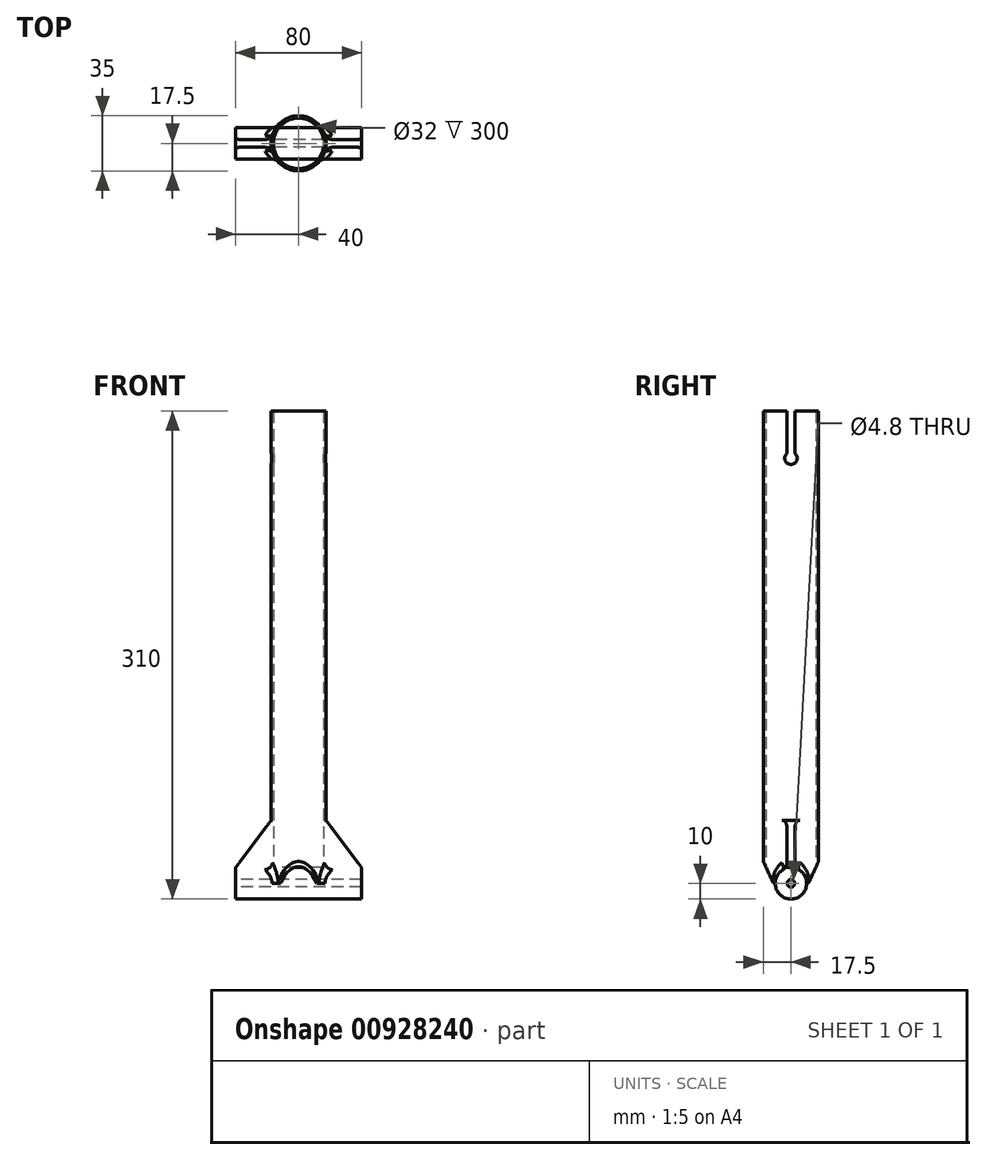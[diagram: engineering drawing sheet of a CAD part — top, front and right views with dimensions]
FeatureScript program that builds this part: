
annotation { "Feature Type Name" : "Feature", "Feature Type Description" : "" }
export const myFeature = defineFeature(function(context is Context, id is Id, definition is map)
    precondition{}
    {
        {
            var Q0;
            Q0=qCreatedBy(makeId("Right.planeOp"),FACE);
            var sketch = newSketch(context, id + "F0", { "sketchPlane" : qUnion([Q0])});
            skCircle(sketch, "E0", {"center": v(0, 0) * mm, "radius": 10 * mm});
            skSolve(sketch);
        }
        {
            var Q0;
            Q0=qCreatedBy(makeId("Top.planeOp"),FACE);
            var sketch = newSketch(context, id + "F1", { "sketchPlane" : qUnion([Q0])});
            skCircle(sketch, "E1", {"center": v(0, 0) * mm, "radius": 17.5 * mm});
            skCircle(sketch, "E2", {"center": v(0, 0) * mm, "radius": 16 * mm});
            skSolve(sketch);
        }
        {
            var Q0;
            Q0=qCreatedBy(makeId("Front.planeOp"),FACE);
            var sketch = newSketch(context, id + "F2", { "sketchPlane" : qUnion([Q0])});
            skLineSegment(sketch, "E3", {"start": v(-40, 9) * mm, "end": v(-16.45, 9) * mm});
            skLineSegment(sketch, "E4", {"start": v(-16.45, 9) * mm, "end": v(-16.45, 40) * mm});
            skLineSegment(sketch, "E5", {"start": v(-16.45, 40) * mm, "end": v(-17.45, 40) * mm});
            skLineSegment(sketch, "E6", {"start": v(-17.45, 40) * mm, "end": v(-40, 10) * mm});
            skLineSegment(sketch, "E7", {"start": v(-40, 10) * mm, "end": v(-40, 9) * mm});
            skLineSegment(sketch, "E8.MirrorCS", {"start": v(17.45, 40) * mm, "end": v(40, 10) * mm});
            skLineSegment(sketch, "E9.MirrorCS", {"start": v(16.45, 40) * mm, "end": v(17.45, 40) * mm});
            skLineSegment(sketch, "E10.MirrorCS", {"start": v(16.45, 9) * mm, "end": v(16.45, 40) * mm});
            skLineSegment(sketch, "E11.MirrorCS", {"start": v(40, 9) * mm, "end": v(16.45, 9) * mm});
            skLineSegment(sketch, "E12.MirrorCS", {"start": v(40, 10) * mm, "end": v(40, 9) * mm});
            skSolve(sketch);
        }
        {
            var Q0;
            Q0=qCreatedBy(makeId("Right.planeOp"),FACE);
            var sketch = newSketch(context, id + "F3", { "sketchPlane" : qUnion([Q0])});
            skArc(sketch, "E13", {"start": v(-9.06, -4.23) * mm, "mid": v(0, -10) * mm, "end": v(9.06, -4.23) * mm});
            skLineSegment(sketch, "E14", {"start": v(9.06, -4.23) * mm, "end": v(21.74, 22.96) * mm});
            skLineSegment(sketch, "E15", {"start": v(-9.06, -4.23) * mm, "end": v(-21.74, 22.96) * mm});
            skLineSegment(sketch, "E16.0", {"start": v(-18.13, -8.45) * mm, "end": v(-30.8, 18.74) * mm});
            skArc(sketch, "E16.1", {"start": v(-18.13, -8.45) * mm, "mid": v(0, -20) * mm, "end": v(18.13, -8.45) * mm});
            skLineSegment(sketch, "E16.2", {"start": v(18.13, -8.45) * mm, "end": v(30.8, 18.74) * mm});
            skLineSegment(sketch, "E17", {"start": v(-30.8, 18.74) * mm, "end": v(-21.74, 22.96) * mm});
            skLineSegment(sketch, "E18", {"start": v(21.74, 22.96) * mm, "end": v(30.8, 18.74) * mm});
            skSolve(sketch);
        }
        {
            var Q0;
            Q0=qCreatedBy(makeId("Right.planeOp"),FACE);
            var sketch = newSketch(context, id + "F4", { "sketchPlane" : qUnion([Q0])});
            skCircle(sketch, "E19", {"center": v(0, 0) * mm, "radius": 2.4 * mm});
            skSolve(sketch);
        }
        {
            var Q0;
            Q0=qCreatedBy(makeId("Right.planeOp"),FACE);
            var sketch = newSketch(context, id + "F5", { "sketchPlane" : qUnion([Q0])});
            skArc(sketch, "E20", {"start": v(-2.5, 273.12) * mm, "mid": v(0, 266) * mm, "end": v(2.5, 273.12) * mm});
            skArc(sketch, "E21.0.endCap", {"start": v(-2.5, 310) * mm, "mid": v(0, 312.5) * mm, "end": v(2.5, 310) * mm});
            skLineSegment(sketch, "E21.0.left", {"start": v(-2.5, 273.12) * mm, "end": v(-2.5, 310) * mm});
            skLineSegment(sketch, "E21.0.right", {"start": v(2.5, 273.12) * mm, "end": v(2.5, 310) * mm});
            skSolve(sketch);
        }
        {
            var Q0;
            Q0=qSketchRegion(id+"F0",true);
            extrude(context, id + "F6", {"entities" : qUnion([Q0]), "endBound" : BoundingType.SYMMETRIC, "depth" : 80 * mm, "offsetDistance" : 25 * mm});
        }
        {
            var Q0;
            Q0=qSketchRegion(id+"F1",true);
            extrude(context, id + "F7", {"entities" : qUnion([Q0]), "operationType" : NewBodyOperationType.ADD, "depth" : 300 * mm, "offsetDistance" : 25 * mm});
        }
        {
            var Q0;
            Q0=qSketchRegion(id+"F2",true);
            extrude(context, id + "F8", {"entities" : qUnion([Q0]), "operationType" : NewBodyOperationType.ADD, "endBound" : BoundingType.SYMMETRIC, "depth" : 5 * mm, "offsetDistance" : 25 * mm});
        }
        {
            var Q0;
            Q0=qSketchRegion(id+"F3",true);
            extrude(context, id + "F9", {"entities" : qUnion([Q0]), "operationType" : NewBodyOperationType.REMOVE, "endBound" : BoundingType.SYMMETRIC, "depth" : 80 * mm, "offsetDistance" : 25 * mm});
        }
        {
            var Q0;
            Q0=qSketchRegion(id+"F4",true);
            extrude(context, id + "F10", {"entities" : qUnion([Q0]), "operationType" : NewBodyOperationType.REMOVE, "endBound" : BoundingType.SYMMETRIC, "depth" : 80 * mm, "offsetDistance" : 25 * mm});
        }
        {
            var Q0;
            Q0=makeQuery(id+"F8.boolean.opBoolean","INTERSECT",EDGE,{"derivedFrom":[makeQuery(id+"F7.opExtrude","SWEPT_FACE",FACE,{"disambiguationData":[OSD([sQuery(id+"F1.wireOp",EDGE,"E1")])]}),makeQuery(id+"F8.opExtrude","CAP_FACE",FACE,{"disambiguationData":[OSD([sQuery(id+"F2.wireOp",EDGE,"E8.MirrorCS"),sQuery(id+"F2.wireOp",EDGE,"E9.MirrorCS"),sQuery(id+"F2.wireOp",EDGE,"E10.MirrorCS"),sQuery(id+"F2.wireOp",EDGE,"E11.MirrorCS"),sQuery(id+"F2.wireOp",EDGE,"E12.MirrorCS")])],"isStart":false})]});
            var Q1;
            Q1=makeQuery(id+"F8.boolean.opBoolean","INTERSECT",EDGE,{"derivedFrom":[makeQuery(id+"F6.opExtrude","SWEPT_FACE",FACE,{"disambiguationData":[OSD([sQuery(id+"F0.wireOp",EDGE,"E0")])]}),makeQuery(id+"F8.opExtrude","CAP_FACE",FACE,{"disambiguationData":[OSD([sQuery(id+"F2.wireOp",EDGE,"E8.MirrorCS"),sQuery(id+"F2.wireOp",EDGE,"E9.MirrorCS"),sQuery(id+"F2.wireOp",EDGE,"E10.MirrorCS"),sQuery(id+"F2.wireOp",EDGE,"E11.MirrorCS"),sQuery(id+"F2.wireOp",EDGE,"E12.MirrorCS")])],"isStart":false})]});
            var Q2;
            Q2=makeQuery(id+"F8.boolean.opBoolean","INTERSECT",EDGE,{"derivedFrom":[makeQuery(id+"F7.opExtrude","SWEPT_FACE",FACE,{"disambiguationData":[OSD([sQuery(id+"F1.wireOp",EDGE,"E1")])]}),makeQuery(id+"F8.opExtrude","CAP_FACE",FACE,{"disambiguationData":[OSD([sQuery(id+"F2.wireOp",EDGE,"E8.MirrorCS"),sQuery(id+"F2.wireOp",EDGE,"E9.MirrorCS"),sQuery(id+"F2.wireOp",EDGE,"E10.MirrorCS"),sQuery(id+"F2.wireOp",EDGE,"E11.MirrorCS"),sQuery(id+"F2.wireOp",EDGE,"E12.MirrorCS")])],"isStart":true})]});
            var Q3;
            Q3=makeQuery(id+"F8.boolean.opBoolean","INTERSECT",EDGE,{"derivedFrom":[makeQuery(id+"F6.opExtrude","SWEPT_FACE",FACE,{"disambiguationData":[OSD([sQuery(id+"F0.wireOp",EDGE,"E0")])]}),makeQuery(id+"F8.opExtrude","CAP_FACE",FACE,{"disambiguationData":[OSD([sQuery(id+"F2.wireOp",EDGE,"E8.MirrorCS"),sQuery(id+"F2.wireOp",EDGE,"E9.MirrorCS"),sQuery(id+"F2.wireOp",EDGE,"E10.MirrorCS"),sQuery(id+"F2.wireOp",EDGE,"E11.MirrorCS"),sQuery(id+"F2.wireOp",EDGE,"E12.MirrorCS")])],"isStart":true})]});
            var Q4;
            Q4=makeQuery(id+"F8.boolean.opBoolean","INTERSECT",EDGE,{"derivedFrom":[makeQuery(id+"F6.opExtrude","SWEPT_FACE",FACE,{"disambiguationData":[OSD([sQuery(id+"F0.wireOp",EDGE,"E0")])]}),makeQuery(id+"F8.opExtrude","CAP_FACE",FACE,{"disambiguationData":[OSD([sQuery(id+"F2.wireOp",EDGE,"E3"),sQuery(id+"F2.wireOp",EDGE,"E4"),sQuery(id+"F2.wireOp",EDGE,"E5"),sQuery(id+"F2.wireOp",EDGE,"E6"),sQuery(id+"F2.wireOp",EDGE,"E7")])],"isStart":true})]});
            var Q5;
            Q5=makeQuery(id+"F8.boolean.opBoolean","INTERSECT",EDGE,{"derivedFrom":[makeQuery(id+"F7.opExtrude","SWEPT_FACE",FACE,{"disambiguationData":[OSD([sQuery(id+"F1.wireOp",EDGE,"E1")])]}),makeQuery(id+"F8.opExtrude","CAP_FACE",FACE,{"disambiguationData":[OSD([sQuery(id+"F2.wireOp",EDGE,"E3"),sQuery(id+"F2.wireOp",EDGE,"E4"),sQuery(id+"F2.wireOp",EDGE,"E5"),sQuery(id+"F2.wireOp",EDGE,"E6"),sQuery(id+"F2.wireOp",EDGE,"E7")])],"isStart":true})]});
            var Q6;
            Q6=makeQuery(id+"F8.boolean.opBoolean","INTERSECT",EDGE,{"derivedFrom":[makeQuery(id+"F7.opExtrude","SWEPT_FACE",FACE,{"disambiguationData":[OSD([sQuery(id+"F1.wireOp",EDGE,"E1")])]}),makeQuery(id+"F8.opExtrude","CAP_FACE",FACE,{"disambiguationData":[OSD([sQuery(id+"F2.wireOp",EDGE,"E3"),sQuery(id+"F2.wireOp",EDGE,"E4"),sQuery(id+"F2.wireOp",EDGE,"E5"),sQuery(id+"F2.wireOp",EDGE,"E6"),sQuery(id+"F2.wireOp",EDGE,"E7")])],"isStart":false})]});
            var Q7;
            Q7=makeQuery(id+"F8.boolean.opBoolean","INTERSECT",EDGE,{"derivedFrom":[makeQuery(id+"F6.opExtrude","SWEPT_FACE",FACE,{"disambiguationData":[OSD([sQuery(id+"F0.wireOp",EDGE,"E0")])]}),makeQuery(id+"F8.opExtrude","CAP_FACE",FACE,{"disambiguationData":[OSD([sQuery(id+"F2.wireOp",EDGE,"E3"),sQuery(id+"F2.wireOp",EDGE,"E4"),sQuery(id+"F2.wireOp",EDGE,"E5"),sQuery(id+"F2.wireOp",EDGE,"E6"),sQuery(id+"F2.wireOp",EDGE,"E7")])],"isStart":false})]});
            var Q8;
            {var subQ0=makeQuery(id+"F6.opExtrude","SWEPT_FACE",FACE,{"disambiguationData":[OSD([sQuery(id+"F0.wireOp",EDGE,"E0")])]});var subQ1=sQuery(id+"F1.wireOp",EDGE,"E1");var subQ2=makeQuery(id+"F7.opExtrude","SWEPT_FACE",FACE,{"disambiguationData":[OSD([subQ1])]});Q8=makeQuery(id+"F8.boolean.opBoolean","SPLIT",EDGE,{"disambiguationData":[TD([makeQuery(id+"F8.opExtrude","CAP_FACE",FACE,{"disambiguationData":[OSD([sQuery(id+"F2.wireOp",EDGE,"E3"),sQuery(id+"F2.wireOp",EDGE,"E4"),sQuery(id+"F2.wireOp",EDGE,"E5"),sQuery(id+"F2.wireOp",EDGE,"E6"),sQuery(id+"F2.wireOp",EDGE,"E7")])],"isStart":true})])],"derivedFrom":makeQuery(id+"F7.boolean.opBoolean","INTERSECT",EDGE,{"disambiguationData":[OD(0.0)],"derivedFrom":[subQ0,subQ2]})});}
            var Q9;
            {var subQ0=makeQuery(id+"F6.opExtrude","SWEPT_FACE",FACE,{"disambiguationData":[OSD([sQuery(id+"F0.wireOp",EDGE,"E0")])]});var subQ1=sQuery(id+"F1.wireOp",EDGE,"E1");var subQ2=makeQuery(id+"F7.opExtrude","SWEPT_FACE",FACE,{"disambiguationData":[OSD([subQ1])]});Q9=makeQuery(id+"F8.boolean.opBoolean","SPLIT",EDGE,{"disambiguationData":[TD([makeQuery(id+"F8.opExtrude","CAP_FACE",FACE,{"disambiguationData":[OSD([sQuery(id+"F2.wireOp",EDGE,"E8.MirrorCS"),sQuery(id+"F2.wireOp",EDGE,"E9.MirrorCS"),sQuery(id+"F2.wireOp",EDGE,"E10.MirrorCS"),sQuery(id+"F2.wireOp",EDGE,"E11.MirrorCS"),sQuery(id+"F2.wireOp",EDGE,"E12.MirrorCS")])],"isStart":true})])],"derivedFrom":makeQuery(id+"F7.boolean.opBoolean","INTERSECT",EDGE,{"disambiguationData":[OD(1.0)],"derivedFrom":[subQ0,subQ2]})});}
            var Q10;
            {var subQ0=makeQuery(id+"F6.opExtrude","SWEPT_FACE",FACE,{"disambiguationData":[OSD([sQuery(id+"F0.wireOp",EDGE,"E0")])]});var subQ1=sQuery(id+"F1.wireOp",EDGE,"E1");var subQ2=makeQuery(id+"F7.opExtrude","SWEPT_FACE",FACE,{"disambiguationData":[OSD([subQ1])]});Q10=makeQuery(id+"F8.boolean.opBoolean","SPLIT",EDGE,{"disambiguationData":[TD([makeQuery(id+"F8.opExtrude","CAP_FACE",FACE,{"disambiguationData":[OSD([sQuery(id+"F2.wireOp",EDGE,"E8.MirrorCS"),sQuery(id+"F2.wireOp",EDGE,"E9.MirrorCS"),sQuery(id+"F2.wireOp",EDGE,"E10.MirrorCS"),sQuery(id+"F2.wireOp",EDGE,"E11.MirrorCS"),sQuery(id+"F2.wireOp",EDGE,"E12.MirrorCS")])],"isStart":false})])],"derivedFrom":makeQuery(id+"F7.boolean.opBoolean","INTERSECT",EDGE,{"disambiguationData":[OD(1.0)],"derivedFrom":[subQ0,subQ2]})});}
            var Q11;
            {var subQ0=makeQuery(id+"F6.opExtrude","SWEPT_FACE",FACE,{"disambiguationData":[OSD([sQuery(id+"F0.wireOp",EDGE,"E0")])]});var subQ1=sQuery(id+"F1.wireOp",EDGE,"E1");var subQ2=makeQuery(id+"F7.opExtrude","SWEPT_FACE",FACE,{"disambiguationData":[OSD([subQ1])]});Q11=makeQuery(id+"F8.boolean.opBoolean","SPLIT",EDGE,{"disambiguationData":[TD([makeQuery(id+"F8.opExtrude","CAP_FACE",FACE,{"disambiguationData":[OSD([sQuery(id+"F2.wireOp",EDGE,"E3"),sQuery(id+"F2.wireOp",EDGE,"E4"),sQuery(id+"F2.wireOp",EDGE,"E5"),sQuery(id+"F2.wireOp",EDGE,"E6"),sQuery(id+"F2.wireOp",EDGE,"E7")])],"isStart":false})])],"derivedFrom":makeQuery(id+"F7.boolean.opBoolean","INTERSECT",EDGE,{"disambiguationData":[OD(0.0)],"derivedFrom":[subQ0,subQ2]})});}
            fillet(context, id + "F11", {"entities" : qUnion([Q0, Q1, Q2, Q3, Q4, Q5, Q6, Q7, Q8, Q9, Q10, Q11]), "radius" : 5 * mm, "tangentPropagation" : true});
        }
        {
            var Q0;
            Q0=qSketchRegion(id+"F5",true);
            extrude(context, id + "F12", {"entities" : qUnion([Q0]), "operationType" : NewBodyOperationType.REMOVE, "endBound" : BoundingType.SYMMETRIC, "depth" : 50 * mm, "offsetDistance" : 25 * mm});
        }
    });
